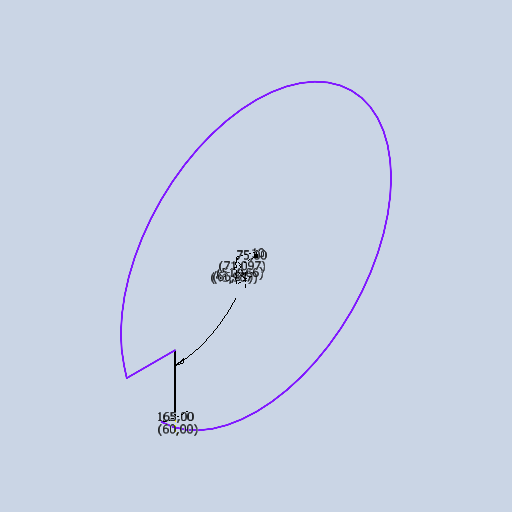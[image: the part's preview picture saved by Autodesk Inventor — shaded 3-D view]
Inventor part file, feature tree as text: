
AUTODESK INVENTOR PART (.ipt)
format: ipt  version: 2025 (Build 290162010, 162A)  size: 96,256 bytes
history: native  units: mm
features: other x4, reference x2, sketch x1
ambient origin geometry x8: Origin, YZ Plane, XZ Plane, XY Plane, X Axis, Y Axis, Z Axis, Center Point
feature tree (7):
  sketch  "Skizze1"  dims[d1=60.0deg d2=66.509973mm d3=71.096646mm d4=51.165823mm d5=41.90731mm d6=75.0deg d7=10.0mm d8=165.0deg]
  reference  "Referenz2"
  reference  "Referenz3"
  other  "<userpath>\GIT\HDVKBM\CAD\Krandemonstrator\Demonstrator.iam"
  other  "Demonstrator.iam"
  other  "Schlitten:1"
  other  "SchlittenS:1"
